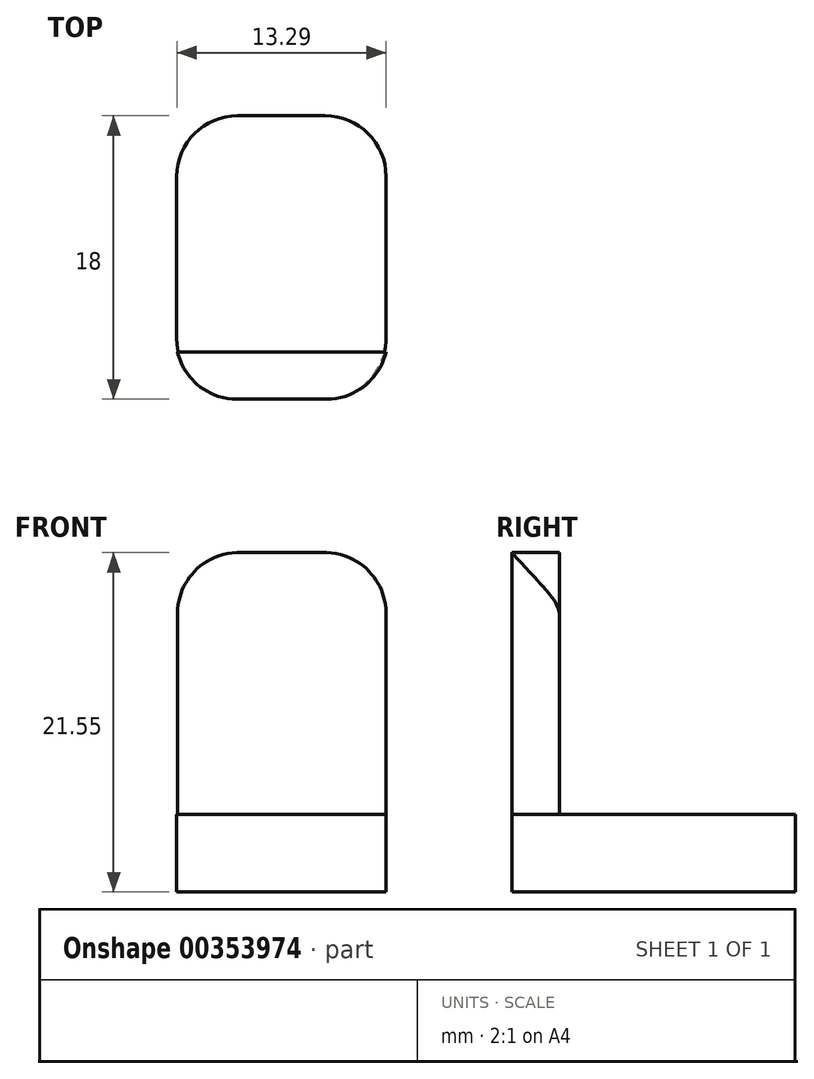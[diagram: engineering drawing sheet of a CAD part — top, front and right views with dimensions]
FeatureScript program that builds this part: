
annotation { "Feature Type Name" : "Feature", "Feature Type Description" : "" }
export const myFeature = defineFeature(function(context is Context, id is Id, definition is map)
    precondition{}
    {
        {
            var Q0;
            Q0=qCreatedBy(makeId("Front.planeOp"),FACE);
            var sketch = newSketch(context, id + "F0", { "sketchPlane" : qUnion([Q0])});
            skLineSegment(sketch, "E0.bottom", {"start": v(-37.34, -31.54) * mm, "end": v(-24.05, -31.54) * mm});
            skLineSegment(sketch, "E0.top", {"start": v(-37.34, -36.47) * mm, "end": v(-24.05, -36.47) * mm});
            skLineSegment(sketch, "E0.left", {"start": v(-37.34, -31.54) * mm, "end": v(-37.34, -36.47) * mm});
            skLineSegment(sketch, "E0.right", {"start": v(-24.05, -31.54) * mm, "end": v(-24.05, -36.47) * mm});
            skSolve(sketch);
        }
        {
            var Q0;
            Q0 = qSketchRegion(id + "F0", true);
            extrude(context, id + "F1", {"entities" : qUnion([Q0]), "oppositeDirection" : true, "depth" : 18 * mm});
        }
        {
            var Q0;
            Q0=qCreatedBy(makeId("Front.planeOp"),FACE);
            var sketch = newSketch(context, id + "F2", { "sketchPlane" : qUnion([Q0])});
            skLineSegment(sketch, "E1.bottom", {"start": v(-24.05, -31.54) * mm, "end": v(-37.3, -31.54) * mm});
            skLineSegment(sketch, "E1.top", {"start": v(-24.05, -14.92) * mm, "end": v(-37.3, -14.92) * mm});
            skLineSegment(sketch, "E1.left", {"start": v(-24.05, -31.54) * mm, "end": v(-24.05, -14.92) * mm});
            skLineSegment(sketch, "E1.right", {"start": v(-37.3, -31.54) * mm, "end": v(-37.3, -14.92) * mm});
            skSolve(sketch);
        }
        {
            var Q0;
            Q0 = qSketchRegion(id + "F2", true);
            extrude(context, id + "F3", {"entities" : qUnion([Q0]), "oppositeDirection" : true, "depth" : 3 * mm});
        }
        {
            var Q0;
            Q0=makeQuery(id+"F3.opExtrude","SWEPT_EDGE",EDGE,{"disambiguationData":[OSD([sQuery(id+"F2.wireOp",EDGE,"E1.top"),sQuery(id+"F2.wireOp",EDGE,"E1.left")])]});
            var Q1;
            Q1=makeQuery(id+"F3.opExtrude","SWEPT_EDGE",EDGE,{"disambiguationData":[OSD([sQuery(id+"F2.wireOp",EDGE,"E1.top"),sQuery(id+"F2.wireOp",EDGE,"E1.right")])]});
            var Q2;
            Q2=makeQuery(id+"F1.opExtrude","CAP_EDGE",EDGE,{"disambiguationData":[OSD([sQuery(id+"F0.wireOp",EDGE,"E0.left")])],"isStart":false});
            var Q3;
            Q3=makeQuery(id+"F1.opExtrude","CAP_EDGE",EDGE,{"disambiguationData":[OSD([sQuery(id+"F0.wireOp",EDGE,"E0.right")])],"isStart":false});
            var Q4;
            Q4=makeQuery(id+"F1.opExtrude","CAP_EDGE",EDGE,{"disambiguationData":[OSD([sQuery(id+"F0.wireOp",EDGE,"E0.left")])],"isStart":true});
            var Q5;
            Q5=makeQuery(id+"F1.opExtrude","CAP_EDGE",EDGE,{"disambiguationData":[OSD([sQuery(id+"F0.wireOp",EDGE,"E0.right")])],"isStart":true});
            var Q6;
            Q6=makeQuery(id+"F3.opExtrude","CAP_EDGE",EDGE,{"disambiguationData":[OSD([sQuery(id+"F2.wireOp",EDGE,"E1.left")])],"isStart":true});
            var Q7;
            Q7=makeQuery(id+"F3.opExtrude","CAP_EDGE",EDGE,{"disambiguationData":[OSD([sQuery(id+"F2.wireOp",EDGE,"E1.right")])],"isStart":true});
            fillet(context, id + "F4", {"entities" : qUnion([Q0, Q1, Q2, Q3, Q4, Q5, Q6, Q7]), "radius" : 3.86 * mm, "tangentPropagation" : true, "allowEdgeOverflow" : false});
        }
    });
